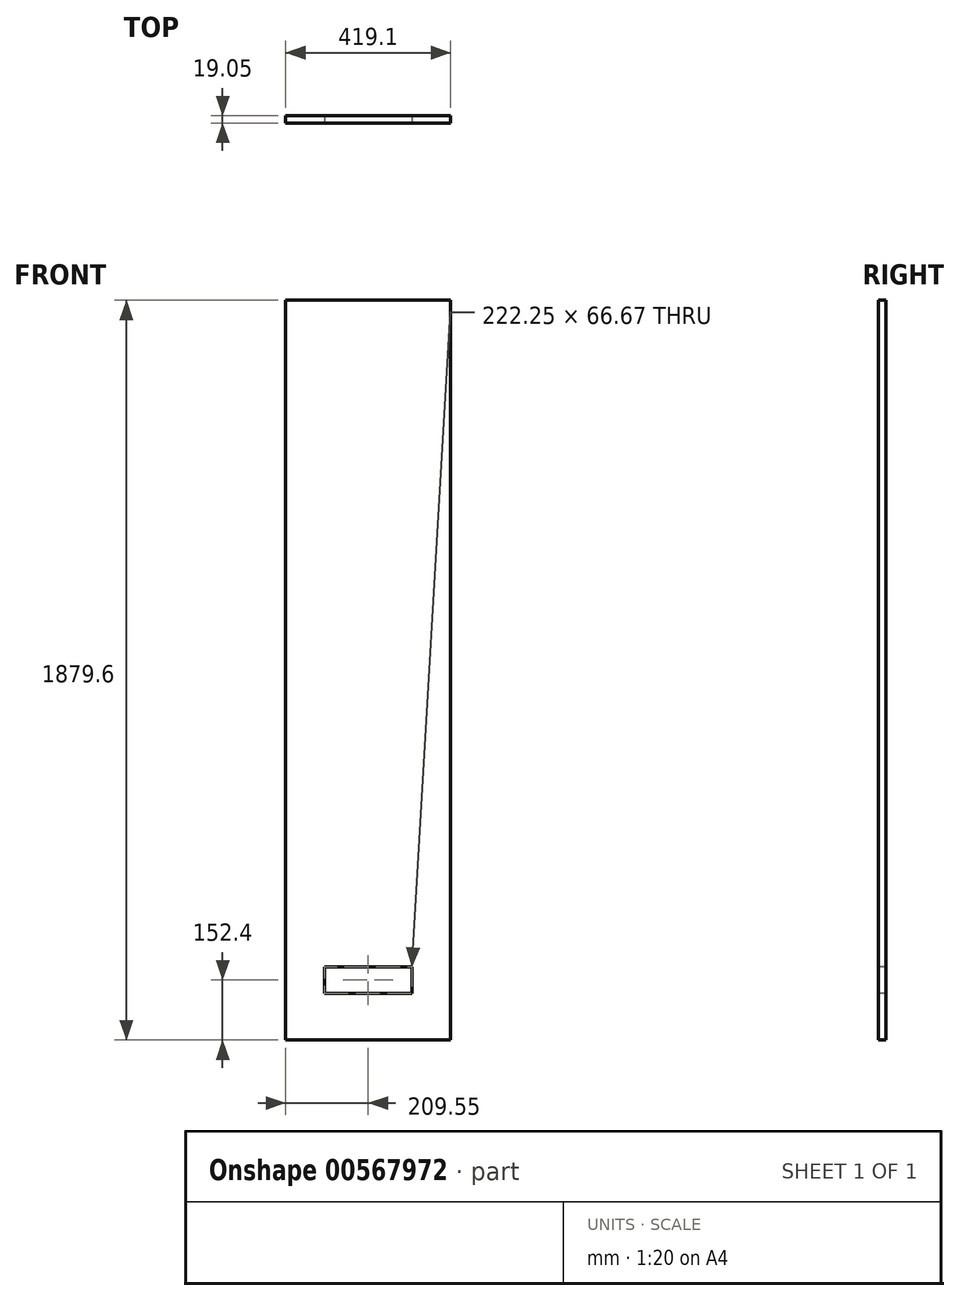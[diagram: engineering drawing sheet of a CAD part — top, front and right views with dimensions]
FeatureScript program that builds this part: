
annotation { "Feature Type Name" : "Feature", "Feature Type Description" : "" }
export const myFeature = defineFeature(function(context is Context, id is Id, definition is map)
    precondition{}
    {
        {
            var Q0;
            Q0=qCreatedBy(makeId("Front.planeOp"),FACE);
            var sketch = newSketch(context, id + "F0", { "sketchPlane" : qUnion([Q0])});
            skLineSegment(sketch, "E0.bottom", {"start": v(209.55, 939.8) * mm, "end": v(-209.55, 939.8) * mm});
            skLineSegment(sketch, "E0.top", {"start": v(209.55, -939.8) * mm, "end": v(-209.55, -939.8) * mm});
            skLineSegment(sketch, "E0.left", {"start": v(209.55, 939.8) * mm, "end": v(209.55, -939.8) * mm});
            skLineSegment(sketch, "E0.right", {"start": v(-209.55, 939.8) * mm, "end": v(-209.55, -939.8) * mm});
            skPoint(sketch, "E0.middle", {"position": v(0, 0) * mm});
            skSolve(sketch);
        }
        {
            var Q0;
            Q0=makeQuery(id+"F0.imprint","IMPRINT",FACE,{"disambiguationData":[TD([[makeQuery(id+"F0.imprint","IMPRINT",EDGE,{"derivedFrom":sQuery(id+"F0.wireOp",EDGE,"E0.bottom")}),1.0]])]});
            extrude(context, id + "F1", {"entities" : qUnion([Q0]), "depth" : 19.05 * mm, "offsetDistance" : 25.4 * mm});
        }
        {
            var Q0;
            Q0=makeQuery(id+"F1.opExtrude","CAP_FACE",FACE,{"disambiguationData":[OSD([sQuery(id+"F0.wireOp",EDGE,"E0.bottom"),sQuery(id+"F0.wireOp",EDGE,"E0.top"),sQuery(id+"F0.wireOp",EDGE,"E0.left"),sQuery(id+"F0.wireOp",EDGE,"E0.right")])],"isStart":false});
            var sketch = newSketch(context, id + "F2", { "sketchPlane" : qUnion([Q0])});
            skLineSegment(sketch, "E1", {"start": v(0, -939.8) * mm, "end": v(0, -787.4) * mm});
            skPoint(sketch, "E1.endSnap0", {"position": v(0, -939.8) * mm});
            skLineSegment(sketch, "E2.bottom", {"start": v(111.12, -754.06) * mm, "end": v(-111.13, -754.06) * mm});
            skLineSegment(sketch, "E2.top", {"start": v(111.13, -820.74) * mm, "end": v(-111.13, -820.74) * mm});
            skLineSegment(sketch, "E2.left", {"start": v(111.12, -754.06) * mm, "end": v(111.13, -820.74) * mm});
            skLineSegment(sketch, "E2.right", {"start": v(-111.13, -754.06) * mm, "end": v(-111.13, -820.74) * mm});
            skPoint(sketch, "E2.middle", {"position": v(0, -787.4) * mm});
            skSolve(sketch);
        }
        {
            var Q0;
            Q0=makeQuery(id+"F2.imprint","IMPRINT",FACE,{"disambiguationData":[TD([[makeQuery(id+"F2.imprint","IMPRINT",EDGE,{"derivedFrom":sQuery(id+"F2.wireOp",EDGE,"E2.bottom")}),1.0]])]});
            extrude(context, id + "F3", {"entities" : qUnion([Q0]), "operationType" : NewBodyOperationType.REMOVE, "oppositeDirection" : true, "depth" : 25.4 * mm, "offsetDistance" : 25.4 * mm});
        }
    });
